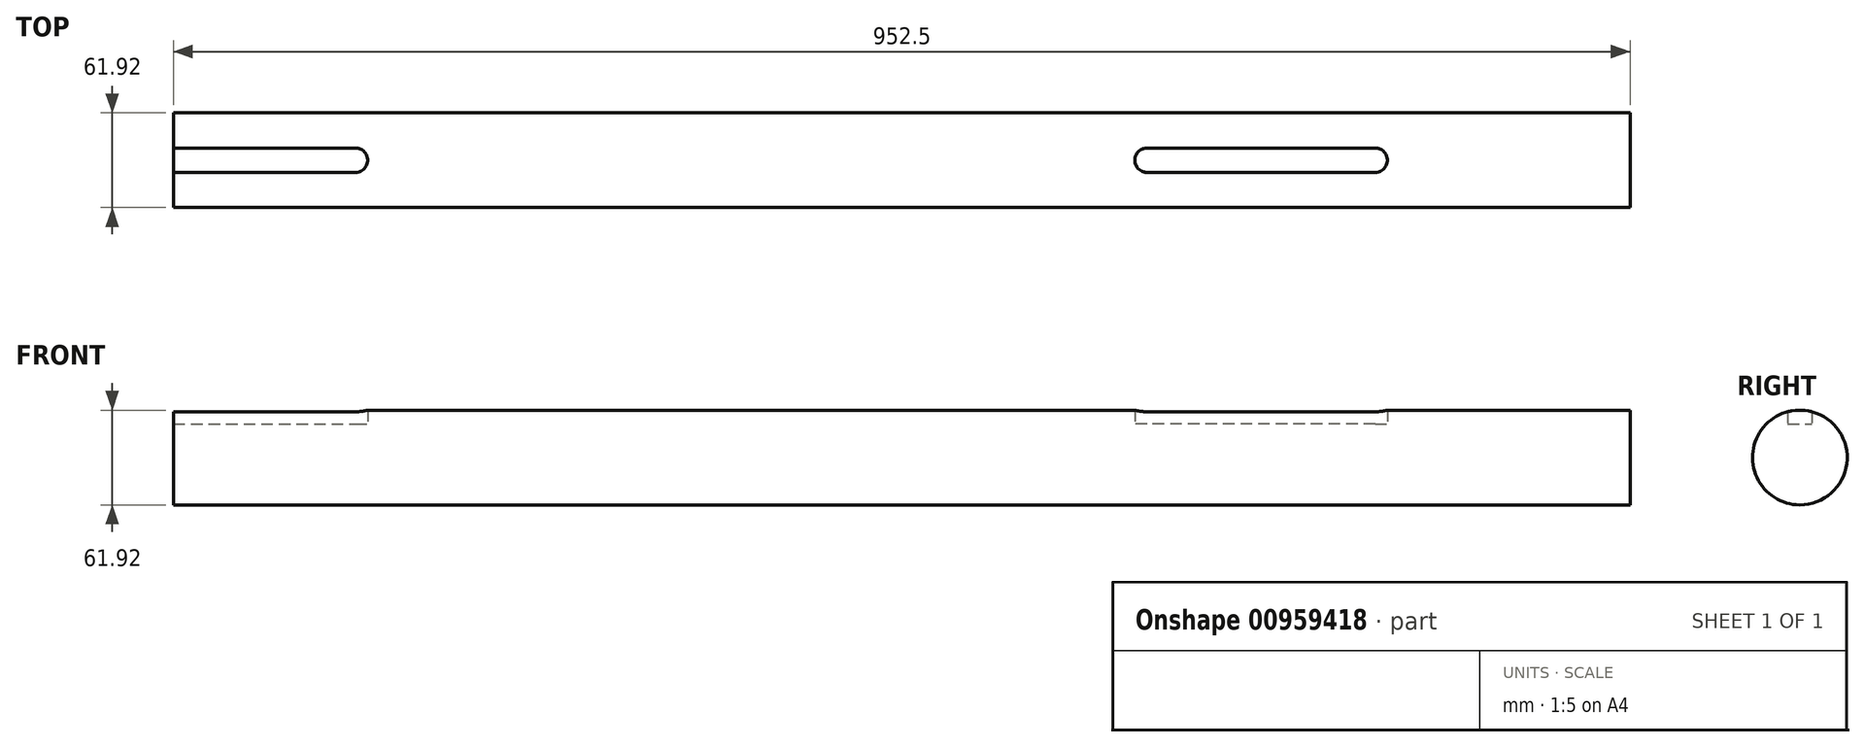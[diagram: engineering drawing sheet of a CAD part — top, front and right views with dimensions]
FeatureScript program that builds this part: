
annotation { "Feature Type Name" : "Feature", "Feature Type Description" : "" }
export const myFeature = defineFeature(function(context is Context, id is Id, definition is map)
    precondition{}
    {
        {
            var Q0;
            Q0=qCreatedBy(makeId("Right.planeOp"),FACE);
            var sketch = newSketch(context, id + "F0", { "sketchPlane" : qUnion([Q0])});
            skCircle(sketch, "E0", {"center": v(0, 0) * mm, "radius": 30.96 * mm});
            skSolve(sketch);
        }
        {
            var Q0;
            Q0=makeQuery(id+"F0.imprint","IMPRINT",FACE,{"disambiguationData":[TD([[makeQuery(id+"F0.imprint","IMPRINT",EDGE,{"derivedFrom":sQuery(id+"F0.wireOp",EDGE,"E0")}),1.0]])]});
            var Q1;
            Q1=sQuery(id+"F0.wireOp",EDGE,"E0");
            extrude(context, id + "F1", {"entities" : qUnion([Q0]), "surfaceEntities" : qUnion([Q1]), "depth" : 952.5 * mm, "offsetDistance" : 25.4 * mm});
        }
        {
            var Q0;
            Q0=qCreatedBy(makeId("Right.planeOp"),FACE);
            var sketch = newSketch(context, id + "F2", { "sketchPlane" : qUnion([Q0])});
            skCircle(sketch, "E1.0", {"center": v(0, 0) * mm, "radius": 30.96 * mm, "construction": true});
            skLineSegment(sketch, "E2", {"start": v(0, 29.92) * mm, "end": v(-7.94, 29.92) * mm});
            skLineSegment(sketch, "E3", {"start": v(0, 29.92) * mm, "end": v(7.94, 29.92) * mm});
            skLineSegment(sketch, "E4", {"start": v(7.94, 29.92) * mm, "end": v(7.94, 21.98) * mm});
            skLineSegment(sketch, "E5", {"start": v(7.94, 21.98) * mm, "end": v(-7.94, 21.98) * mm});
            skLineSegment(sketch, "E6", {"start": v(-7.94, 21.98) * mm, "end": v(-7.94, 29.92) * mm});
            skSolve(sketch);
        }
        {
            var Q0;
            Q0=sQuery(id+"F2.wireOp",EDGE,"E5");
            cPoint(context, id + "F3", {"entities" : qUnion([Q0]), "parameter" : 0.5});
        }
        {
            var Q0;
            Q0=qCreatedBy(makeId("Top.planeOp"),FACE);
            var Q1;
            Q1 = qCreatedBy(id + "F3" ,VERTEX);
            cPlane(context, id + "F4", {"entities" : qUnion([Q0, Q1]), "cplaneType" : CPlaneType.PLANE_POINT, "offset" : 25.4 * mm, "width" : 152.4 * mm, "height" : 152.4 * mm});
        }
        {
            var Q0;
            Q0=qCreatedBy(id+"F4.planeOp",FACE);
            var sketch = newSketch(context, id + "F5", { "sketchPlane" : qUnion([Q0])});
            skLineSegment(sketch, "E7", {"start": v(0, 0) * mm, "end": v(0, -7.94) * mm});
            skLineSegment(sketch, "E8", {"start": v(0, -7.94) * mm, "end": v(119.06, -7.94) * mm});
            skCircle(sketch, "E9", {"center": v(119.06, 0) * mm, "radius": 7.94 * mm});
            skCircle(sketch, "E10", {"center": v(636.59, 0) * mm, "radius": 7.94 * mm});
            skCircle(sketch, "E11", {"center": v(785.81, 0) * mm, "radius": 7.94 * mm});
            skLineSegment(sketch, "E12", {"start": v(636.59, 7.94) * mm, "end": v(785.81, 7.94) * mm});
            skLineSegment(sketch, "E13", {"start": v(785.81, -7.94) * mm, "end": v(636.59, -7.94) * mm});
            skLineSegment(sketch, "E14", {"start": v(636.59, -7.94) * mm, "end": v(636.59, 0) * mm});
            skLineSegment(sketch, "E15", {"start": v(0, 0) * mm, "end": v(0, 7.94) * mm});
            skLineSegment(sketch, "E16", {"start": v(0, 7.94) * mm, "end": v(119.06, 7.94) * mm});
            skSolve(sketch);
        }
        {
            var Q0;
            Q0 = qSketchRegion(id + "F5", true);
            var Q1;
            Q1=makeQuery(id+"F1.opExtrude","SWEPT_FACE",FACE,{"disambiguationData":[OSD([sQuery(id+"F0.wireOp",EDGE,"E0")])]});
            extrude(context, id + "F6", {"entities" : qUnion([Q0]), "operationType" : NewBodyOperationType.REMOVE, "endBound" : BoundingType.UP_TO_SURFACE, "depth" : 25.4 * mm, "endBoundEntityFace" : qUnion([Q1]), "offsetDistance" : 25.4 * mm});
        }
    });
